# Revit family: 2019_ES_Ventana_QSystems_Q67_2-Hojas
name_source: partatom
category: Windows
units: mm (PartAtom-declared; Revit-internal decimal feet)

## family parameters
Always vertical = Yes
Cut with Voids When Loaded = No
Host = Wall
OmniClass Number = 23.30.20.00
OmniClass Title = Windows
Room Calculation Point = No
Shared = No

## types (4) — shared parameters
Abatible = No
Acabado = Anodizado, lacado y acabados
Acristalamiento = Cristal - Vidrio claro templado
Altura Real = 1480.000 mm
Altura de antepecho por defecto = 500.000 mm
Altura maxima = 2500.000 mm
Altura minima = 600.000 mm
Analytic Construction = 1/4 in Pilkington single glazing
AnchoMarcoCentral = 141.400 mm
AnchoMarcoPerimetral = 89.100 mm
AnchoPoliamidaHoja = 30.000 mm
AnchoPoliamidaMarco = 30.000 mm
Anchura Maxima = 1700.000 mm
Anchura Minima = 100.000 mm
Anchura Real = 1230.000 mm
Area = 1.820 m²
Autor = Bimetica Parametric Design Services, S.L.
BIMsupport = https://bimsupport.info
COBieCategoria = IfcWindow
Catálogo (URL) = https://qsystemsaluminio.com
CerramientoExterior = Yes
Clasificacion acustica = 38 (-1,-4) dB
ConfiguracionPoliamidas = 273800 - 493800 - 493700
ControlHumos = No
CosteEnergeticoMj = 0 J
EspesorPerfilesAluminio = 1.500 mm
EstanqueidadAgua = Clase E900
FechaEmisionElementoBIM = 03/12/2021
FechaVencimientoElementoBIM = 03/12/2022
Fraccion de area de acristalamiento = 0.651043
GrosorAcristalamiento = 24.000 mm
GrosorAcristalamiento Real = 24.000 mm
GrosorHoja = 67.000 mm
GrosorMarco = 60.000 mm
GrosorMaximoAcristalamiento = 46.000 mm
GrosorMinimoAcristalamiento = 12.000 mm
Gubimclass Codigo = 30.10.20.10
Gubimclass Titulo = Ventanas de fachadas
Heat Transfer Coefficient (U) = 6.7018 W/(m²·K)
Height = 1480.000 mm
Historial = (RVT2019) Actualziación a estándar GDO-BIM y datos. (RVT2015) Creación del Elemento.
IfcExportAs = IfcWindow
InformacionTecnica = https://qsystemsaluminio.com
Intercalario = Technoform Warm Edge
Manija = Yes
Manufacturer = QSystems
Marcado CE = No
Marco = Aluminio Anodizado, lacado
MasterformatCodigo = 08 50 00
MasterformatTitulo = Windows
Motorizada = No
Numero de Licencia = XXX-XXXX9536
OmniclassCodigo = 23-17 13 00
OmniclassTitulo = Windows
Perimetro = 5420
PermeabilidadAlAire = Clase 4
Peso = 0.00 kg
PesoMáximoDeLaHoja = 0.00 kg
Plataforma descaga contenido BIM = www.bimetica.com
Poliamida = Technoform polyamide
Porcentaje materiales reciclados = 0.00%
Profundidad = 0.000 mm
PuntoDeContacto = QSystems
Referencia = Q67
ReferenciaContacto = QSystems
RepisaExterior = Yes
RepisaInterior = Yes
ResistenciaAlViento = Clase C5
SalidaEmergencia = No
Serie = Q67
Solar Heat Gain Coefficient = 0.86
TelefonoContacto = +34 91 895 58 00
Thermal Resistance (R) = 0.1492 (m²·K)/W
Titular = Alueuropa S.A.
Total Y𝑔 = 0.11
Total 𝐴𝑓 = 0.635241
Total 𝐴𝑔 = 1.185159
Total 𝑈𝑔 = 1.5
Total 𝑙𝑔 = 7.028
UNSPSCCodigo = 30171600
UNSPSCTitulo = Windows
URL = http://qsystemsaluminio.com
URL Perfil BIM = https://bimetica.com
URL Poliamida = http://www.technoform.es
URL Poliamida - Catálogo = http://www.technoform.com
URLProducto = https://qsystemsaluminio.com
Uniclass2.0Codigo = Ss_15_50_25
Uniclass2.0Titulo = Doors, Windows And Glazing Survey Systems
Version = RVT2019
Version Estandar GDO-BIM = GDO-BIM V02
Visual Light Transmittance = 0.9
Wall Closure = By host
Width = 1230.000 mm
Y𝑔 P1 = 0.11
Y𝑔 P2 = 0.11
𝐴𝑓 P1 = 0.451 m²
𝐴𝑓 P2 = 0.184 m²
𝐴𝑔 V1 = 0.593 m²
𝐴𝑔 V2 = 0.593 m²
𝑈𝑔 V1 = 1.5
𝑈𝑔 V2 = 1.5
𝑙𝑔 P1 = 4.4244
𝑙𝑔 P2 = 2.6036
zero-valued in all types: AcidificacionAtmosferica, AcidificacionAtmosfericaPorUnidad, AguaConsumida, AguaConsumidaPorUnidad, CambioClimatico, CambioClimaticoPorUnidad, CosteEnergeticoKwh, CosteMantenimiento, DestruccionCapaOzonoEstratosferica, DestruccionCapaOzonoEstratosfericaPorUnidad, EmisionCO2, Energia consumida, EnergiaNoRenovableConsumida, EnergiaNoRenovableConsumidaPorUnidad, EnergiaPrimariaTotalConsumida, EnergiaPrimariaTotalConsumidaPorUnidad, EnergiaRenovableConsumida, EnergiaRenovableConsumidaPorUnidad, Eutrofizacion, EutrofizacionPorUnidad, FactorSolarModificado, FactorSombra, FaltaDeRecursos, FaltaDeRecursosPorUnidad, FormacionFotoquimicaOzono, FormacionFotoquimicaOzonoPorUnidad, Infiltracion, MateriaPrima, ResiduoInerte, ResiduoInertePorUnidad, ResiduoRadioactivo, ResiduoRadioactivoPorUnidad, ResiduosNoPeligrosos, ResiduosNoPeligrososPorUnidad, ResiduosPeligrosos, ResiduosPeligrososPorUnidad

## per-type parameters (varying)
| type | Description | Espuma | IfcExportType | Model | Operation | Oscilobatiente | Practicable | Total 𝑈𝑓 | Transmitancia termica | 𝑈𝑓 P1 | 𝑈𝑓 P2 | 𝑈𝑤 |
| 1230x1480 mm - Practicable | Ventana 2 Hojas Practicables Q67 de QSystems |  | Practicable | Ventana Q67 - 2 Hojas Practicable | Practicable. Ventana Practicable de dos hojas con apertura Interior | No | Yes | 2.4 | 2.2387 W/(m²·K) | 2.4 | 2.4 | 2.238737 |
| 1230x1480 mm - Oscilobatiente | Ventana 2 Hojas Oscilobatientes Q67 de QSystems |  | Oscilobatiente | Ventana Q67 - 2 Hojas Oscilobatiente | Oscilobatiente. Ventana Oscilobatiente de dos hojas con apertura Interior | Yes | No | 2.4 | 2.2387 W/(m²·K) | 2.4 | 2.4 | 2.238737 |
| 1230x1480 mm - Oscilobatiente Con Espuma | Ventana 2 Hojas Oscilobatientes  Q67 de QSystems con espuma | Espuma de conductividad 0.021W/mK entre varillas.
Espuma de conductividad 0.034W/mK en el galce del vidrio y en el marco. | Oscilobatiente | Ventana Q67 - 2 Hojas Oscilobatiente | Oscilobatiente. Ventana Oscilobatiente de dos hojas con apertura Interior | Yes | No | 2.1 | 2.1341 W/(m²·K) | 2.1 | 2.1 | 2.13405 |
| 1230x1480 mm - Practicable Con Espuma | Ventana 2 Hojas Practicables Q67 de QSystems con espuma | Espuma de conductividad 0.021W/mK entre varillas.
Espuma de conductividad 0.034W/mK en el galce del vidrio y en el marco. | Practicable | Ventana Q67 - 2 Hojas Practicable | Practicable. Ventana Practicable de dos hojas con apertura Interior | No | Yes | 2.1 | 2.1341 W/(m²·K) | 2.1 | 2.1 | 2.13405 |

## geometry (parser evidence)
native form markers: Blend x2
no freeform markers — native parametric forms only
